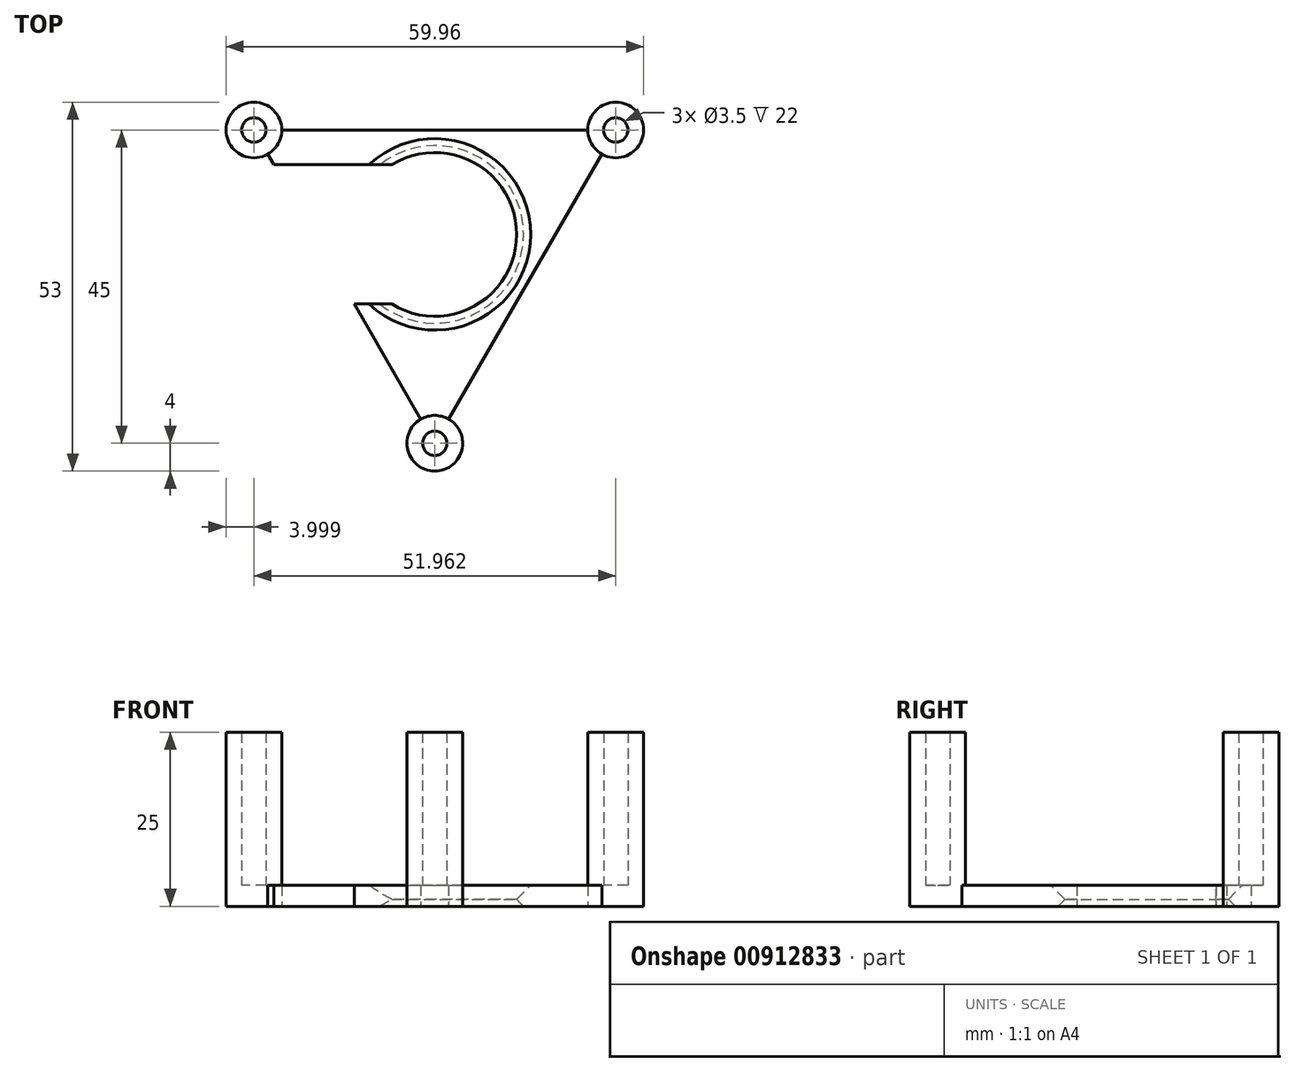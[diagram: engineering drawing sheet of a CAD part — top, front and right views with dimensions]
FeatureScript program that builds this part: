
annotation { "Feature Type Name" : "Feature", "Feature Type Description" : "" }
export const myFeature = defineFeature(function(context is Context, id is Id, definition is map)
    precondition{}
    {
        {
            var Q0;
            Q0=qCreatedBy(makeId("Top.planeOp"),FACE);
            var sketch = newSketch(context, id + "F0", { "sketchPlane" : qUnion([Q0])});
            skCircle(sketch, "E0", {"center": v(0, 0) * mm, "radius": 11.75 * mm});
            skLineSegment(sketch, "E1.bottom", {"start": v(-74.84, 10) * mm, "end": v(75.64, 10) * mm});
            skLineSegment(sketch, "E1.top", {"start": v(-74.84, -10) * mm, "end": v(75.64, -10) * mm});
            skLineSegment(sketch, "E1.left", {"start": v(-74.84, 10) * mm, "end": v(-74.84, -10) * mm});
            skLineSegment(sketch, "E1.right", {"start": v(75.64, 10) * mm, "end": v(75.64, -10) * mm});
            skCircle(sketch, "E2.cCircle", {"center": v(0, 0) * mm, "radius": 15 * mm, "construction": true});
            skLineSegment(sketch, "E2.0", {"start": v(-25.98, 15) * mm, "end": v(25.98, 15) * mm});
            skLineSegment(sketch, "E2.1", {"start": v(25.98, 15) * mm, "end": v(0, -30) * mm});
            skLineSegment(sketch, "E2.2", {"start": v(0, -30) * mm, "end": v(-25.98, 15) * mm});
            skPoint(sketch, "E2.0.midPoint", {"position": v(0, 15) * mm});
            skCircle(sketch, "E3", {"center": v(0, -30) * mm, "radius": 4 * mm});
            skCircle(sketch, "E4.1.0", {"center": v(25.98, 15) * mm, "radius": 4 * mm});
            skCircle(sketch, "E4.2.0", {"center": v(-25.98, 15) * mm, "radius": 4 * mm});
            skCircle(sketch, "E5", {"center": v(0, -30) * mm, "radius": 1.75 * mm});
            skCircle(sketch, "E6.1.0", {"center": v(25.98, 15) * mm, "radius": 1.75 * mm});
            skCircle(sketch, "E6.2.0", {"center": v(-25.98, 15) * mm, "radius": 1.75 * mm});
            skSolve(sketch);
        }
        {
            var Q0;
            {var subQ6=sQuery(id+"F0.wireOp",EDGE,"E1.bottom");var subQ8=sQuery(id+"F0.wireOp",EDGE,"E0");var subQ12=makeQuery(id+"F0.imprint","INTERSECT",VERTEX,{"disambiguationData":[OD(0.0)],"derivedFrom":[subQ8,subQ6]});Q0=makeQuery(id+"F0.imprint","IMPRINT",FACE,{"disambiguationData":[TD([[makeQuery(id+"F0.imprint","IMPRINT",EDGE,{"disambiguationData":[TD([[subQ12,1.0]])],"derivedFrom":subQ8}),-1.0]])]});}
            var Q1;
            {var subQ0=sQuery(id+"F0.wireOp",EDGE,"E1.bottom");var subQ1=sQuery(id+"F0.wireOp",EDGE,"E0");var subQ2=makeQuery(id+"F0.imprint","INTERSECT",VERTEX,{"disambiguationData":[OD(0.0)],"derivedFrom":[subQ1,subQ0]});Q1=makeQuery(id+"F0.imprint","IMPRINT",FACE,{"disambiguationData":[TD([[makeQuery(id+"F0.imprint","IMPRINT",EDGE,{"disambiguationData":[TD([[subQ2,-1.0]])],"derivedFrom":subQ1}),-1.0]])]});}
            var Q2;
            {var subQ1=sQuery(id+"F0.wireOp",EDGE,"E1.top");var subQ3=sQuery(id+"F0.wireOp",EDGE,"E0");var subQ4=makeQuery(id+"F0.imprint","INTERSECT",VERTEX,{"disambiguationData":[OD(0.0)],"derivedFrom":[subQ3,subQ1]});Q2=makeQuery(id+"F0.imprint","IMPRINT",FACE,{"disambiguationData":[TD([[makeQuery(id+"F0.imprint","IMPRINT",EDGE,{"disambiguationData":[TD([[subQ4,-1.0]])],"derivedFrom":subQ3}),-1.0]])]});}
            var Q3;
            {var subQ0=sQuery(id+"F0.wireOp",EDGE,"E1.bottom");var subQ1=sQuery(id+"F0.wireOp",EDGE,"E0");var subQ2=makeQuery(id+"F0.imprint","INTERSECT",VERTEX,{"disambiguationData":[OD(1.0)],"derivedFrom":[subQ1,subQ0]});Q3=makeQuery(id+"F0.imprint","IMPRINT",FACE,{"disambiguationData":[TD([[makeQuery(id+"F0.imprint","IMPRINT",EDGE,{"disambiguationData":[TD([[subQ2,1.0]])],"derivedFrom":subQ1}),-1.0]])]});}
            var Q4;
            {var subQ0=sQuery(id+"F0.wireOp",EDGE,"E2.2");var subQ1=sQuery(id+"F0.wireOp",EDGE,"E2.1");var subQ2=makeQuery(id+"F0.imprint","INTERSECT",VERTEX,{"derivedFrom":[subQ1,subQ0]});Q4=makeQuery(id+"F0.imprint","IMPRINT",FACE,{"disambiguationData":[TD([[makeQuery(id+"F0.imprint","IMPRINT",EDGE,{"disambiguationData":[TD([[subQ2,1.0]])],"derivedFrom":subQ1}),1.0]])]});}
            var Q5;
            {var subQ0=sQuery(id+"F0.wireOp",EDGE,"E2.2");var subQ1=sQuery(id+"F0.wireOp",EDGE,"E2.1");var subQ2=makeQuery(id+"F0.imprint","INTERSECT",VERTEX,{"derivedFrom":[subQ1,subQ0]});Q5=makeQuery(id+"F0.imprint","IMPRINT",FACE,{"disambiguationData":[TD([[makeQuery(id+"F0.imprint","IMPRINT",EDGE,{"disambiguationData":[TD([[subQ2,1.0]])],"derivedFrom":subQ1}),-1.0]])]});}
            var Q6;
            {var subQ0=sQuery(id+"F0.wireOp",EDGE,"E2.1");var subQ1=sQuery(id+"F0.wireOp",EDGE,"E2.0");var subQ2=makeQuery(id+"F0.imprint","INTERSECT",VERTEX,{"derivedFrom":[subQ1,subQ0]});Q6=makeQuery(id+"F0.imprint","IMPRINT",FACE,{"disambiguationData":[TD([[makeQuery(id+"F0.imprint","IMPRINT",EDGE,{"disambiguationData":[TD([[subQ2,1.0]])],"derivedFrom":subQ1}),-1.0]])]});}
            var Q7;
            {var subQ0=sQuery(id+"F0.wireOp",EDGE,"E2.1");var subQ1=sQuery(id+"F0.wireOp",EDGE,"E2.0");var subQ2=makeQuery(id+"F0.imprint","INTERSECT",VERTEX,{"derivedFrom":[subQ1,subQ0]});Q7=makeQuery(id+"F0.imprint","IMPRINT",FACE,{"disambiguationData":[TD([[makeQuery(id+"F0.imprint","IMPRINT",EDGE,{"disambiguationData":[TD([[subQ2,1.0]])],"derivedFrom":subQ1}),1.0]])]});}
            var Q8;
            {var subQ0=sQuery(id+"F0.wireOp",EDGE,"E2.2");var subQ1=sQuery(id+"F0.wireOp",EDGE,"E2.0");var subQ2=makeQuery(id+"F0.imprint","INTERSECT",VERTEX,{"derivedFrom":[subQ1,subQ0]});Q8=makeQuery(id+"F0.imprint","IMPRINT",FACE,{"disambiguationData":[TD([[makeQuery(id+"F0.imprint","IMPRINT",EDGE,{"disambiguationData":[TD([[subQ2,-1.0]])],"derivedFrom":subQ1}),-1.0]])]});}
            var Q9;
            {var subQ0=sQuery(id+"F0.wireOp",EDGE,"E2.2");var subQ1=sQuery(id+"F0.wireOp",EDGE,"E2.0");var subQ2=makeQuery(id+"F0.imprint","INTERSECT",VERTEX,{"derivedFrom":[subQ1,subQ0]});Q9=makeQuery(id+"F0.imprint","IMPRINT",FACE,{"disambiguationData":[TD([[makeQuery(id+"F0.imprint","IMPRINT",EDGE,{"disambiguationData":[TD([[subQ2,-1.0]])],"derivedFrom":subQ1}),1.0]])]});}
            extrude(context, id + "F1", {"entities" : qUnion([Q0, Q1, Q2, Q3, Q4, Q5, Q6, Q7, Q8, Q9]), "depth" : 3 * mm, "offsetDistance" : 25 * mm});
        }
        {
            var Q0;
            {var subQ0=sQuery(id+"F0.wireOp",EDGE,"E4.2.0");var subQ1=sQuery(id+"F0.wireOp",EDGE,"E2.0");var subQ2=makeQuery(id+"F0.imprint","INTERSECT",VERTEX,{"derivedFrom":[subQ1,subQ0]});Q0=makeQuery(id+"F0.imprint","IMPRINT",FACE,{"disambiguationData":[TD([[makeQuery(id+"F0.imprint","IMPRINT",EDGE,{"disambiguationData":[TD([[subQ2,1.0]])],"derivedFrom":subQ1}),-1.0]])]});}
            var Q1;
            {var subQ0=sQuery(id+"F0.wireOp",EDGE,"E4.2.0");var subQ1=sQuery(id+"F0.wireOp",EDGE,"E2.0");var subQ2=makeQuery(id+"F0.imprint","INTERSECT",VERTEX,{"derivedFrom":[subQ1,subQ0]});Q1=makeQuery(id+"F0.imprint","IMPRINT",FACE,{"disambiguationData":[TD([[makeQuery(id+"F0.imprint","IMPRINT",EDGE,{"disambiguationData":[TD([[subQ2,1.0]])],"derivedFrom":subQ1}),1.0]])]});}
            var Q2;
            {var subQ0=sQuery(id+"F0.wireOp",EDGE,"E4.1.0");var subQ1=sQuery(id+"F0.wireOp",EDGE,"E2.0");var subQ2=makeQuery(id+"F0.imprint","INTERSECT",VERTEX,{"derivedFrom":[subQ1,subQ0]});Q2=makeQuery(id+"F0.imprint","IMPRINT",FACE,{"disambiguationData":[TD([[makeQuery(id+"F0.imprint","IMPRINT",EDGE,{"disambiguationData":[TD([[subQ2,-1.0]])],"derivedFrom":subQ1}),-1.0]])]});}
            var Q3;
            {var subQ0=sQuery(id+"F0.wireOp",EDGE,"E4.1.0");var subQ1=sQuery(id+"F0.wireOp",EDGE,"E2.0");var subQ2=makeQuery(id+"F0.imprint","INTERSECT",VERTEX,{"derivedFrom":[subQ1,subQ0]});Q3=makeQuery(id+"F0.imprint","IMPRINT",FACE,{"disambiguationData":[TD([[makeQuery(id+"F0.imprint","IMPRINT",EDGE,{"disambiguationData":[TD([[subQ2,-1.0]])],"derivedFrom":subQ1}),1.0]])]});}
            var Q4;
            {var subQ0=sQuery(id+"F0.wireOp",EDGE,"E3");var subQ1=sQuery(id+"F0.wireOp",EDGE,"E2.1");var subQ2=makeQuery(id+"F0.imprint","INTERSECT",VERTEX,{"derivedFrom":[subQ1,subQ0]});Q4=makeQuery(id+"F0.imprint","IMPRINT",FACE,{"disambiguationData":[TD([[makeQuery(id+"F0.imprint","IMPRINT",EDGE,{"disambiguationData":[TD([[subQ2,-1.0]])],"derivedFrom":subQ1}),-1.0]])]});}
            var Q5;
            {var subQ0=sQuery(id+"F0.wireOp",EDGE,"E3");var subQ1=sQuery(id+"F0.wireOp",EDGE,"E2.1");var subQ2=makeQuery(id+"F0.imprint","INTERSECT",VERTEX,{"derivedFrom":[subQ1,subQ0]});Q5=makeQuery(id+"F0.imprint","IMPRINT",FACE,{"disambiguationData":[TD([[makeQuery(id+"F0.imprint","IMPRINT",EDGE,{"disambiguationData":[TD([[subQ2,-1.0]])],"derivedFrom":subQ1}),1.0]])]});}
            extrude(context, id + "F2", {"entities" : qUnion([Q0, Q1, Q2, Q3, Q4, Q5]), "operationType" : NewBodyOperationType.ADD, "depth" : 25 * mm, "offsetDistance" : 25 * mm});
        }
        {
            var Q0;
            Q0=makeQuery(id+"F1.opExtrude","CAP_EDGE",EDGE,{"disambiguationData":[OSD([sQuery(id+"F0.wireOp",EDGE,"E0")])],"isStart":true});
            chamfer(context, id + "F3", {"entities" : qUnion([Q0]), "width" : 1 * mm, "tangentPropagation" : true});
        }
        {
            var Q0;
            Q0=makeQuery(id+"F1.opExtrude","CAP_EDGE",EDGE,{"disambiguationData":[OSD([sQuery(id+"F0.wireOp",EDGE,"E0")])],"isStart":false});
            chamfer(context, id + "F4", {"entities" : qUnion([Q0]), "width" : 2 * mm, "tangentPropagation" : true});
        }
    });
